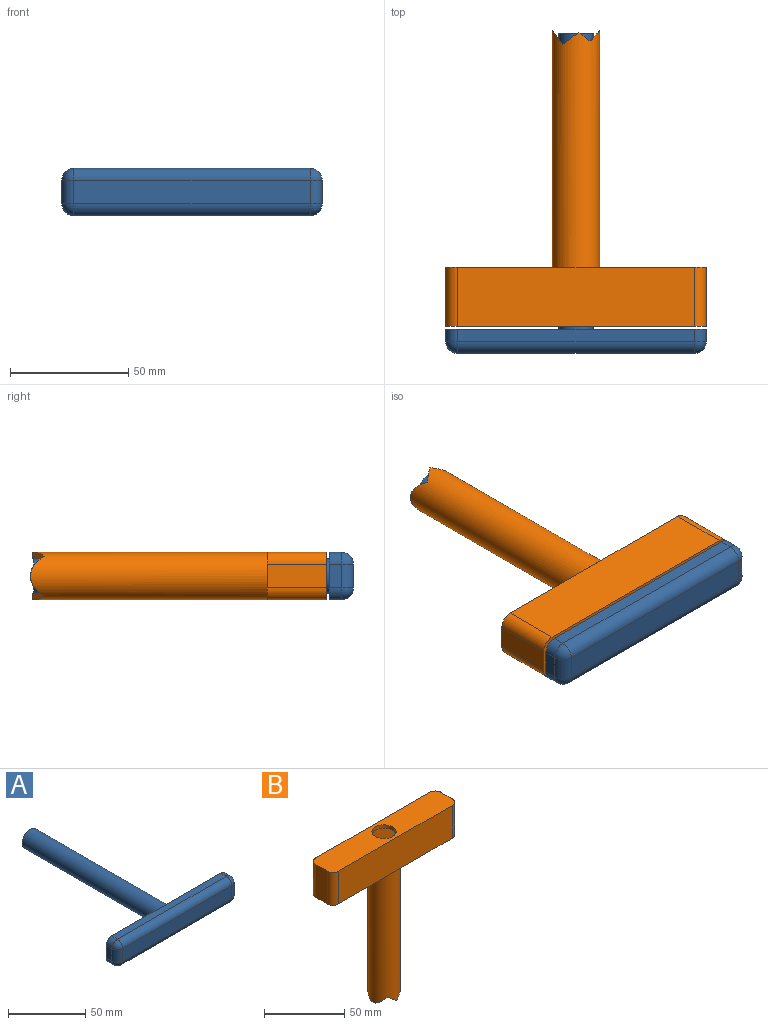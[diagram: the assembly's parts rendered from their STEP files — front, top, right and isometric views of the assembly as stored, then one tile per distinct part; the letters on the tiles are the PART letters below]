
ASSEMBLY  parts=2 mates=1
PART A: 20 faces, bbox 110x135.2x20 mm
  f0: cylinder r=7.25mm len=125mm, axis (0,1,0), area 5694.1mm2, adj f1,f4
  f1: plane 14.5x14.5mm, normal (0,1,0), area 165.1mm2, adj f0
  f2: plane 100x10mm, normal (0,-1,0), area 1000mm2, adj f8,f9,f10,f11
  f3: plane 100x5.23mm, normal (0,0,-1), area 523.4mm2, adj f4,f11,f16,f18
  f4: plane 110x20mm, normal (0,1,0), area 2013.4mm2, adj f0,f3,f5,f6,f7,f12,f14,f16
  f5: plane 100x5.23mm, normal (0,0,1), area 523.4mm2, adj f4,f8,f12,f14
  f6: plane 10x5.23mm, normal (1,0,0), area 52.3mm2, adj f4,f9,f12,f16
  f7: plane 10x5.23mm, normal (-1,0,0), area 52.3mm2, adj f4,f10,f14,f18
  f8: cylinder r=5mm len=100mm, axis (-1,0,0), area 785.4mm2, adj f2,f5,f13,f15
  f9: cylinder r=5mm len=10mm, axis (0,0,1), area 78.5mm2, adj f2,f6,f13,f17
  f10: cylinder r=5mm len=10mm, axis (0,0,-1), area 78.5mm2, adj f2,f7,f15,f19
  f11: cylinder r=5mm len=100mm, axis (1,0,0), area 785.4mm2, adj f2,f3,f17,f19
  f12: cylinder r=5mm len=5.23mm, axis (0,1,0), area 41.1mm2, adj f4,f5,f6,f13
  f13: sphere r=5mm, area 39.3mm2, adj f8,f9,f12
  f14: cylinder r=5mm len=5.23mm, axis (0,-1,0), area 41.1mm2, adj f4,f5,f7,f15
  f15: sphere r=5mm, area 39.3mm2, adj f8,f10,f14
  f16: cylinder r=5mm len=5.23mm, axis (0,-1,0), area 41.1mm2, adj f3,f4,f6,f17
  f17: sphere r=5mm, area 39.3mm2, adj f9,f11,f16
  f18: cylinder r=5mm len=5.23mm, axis (0,1,0), area 41.1mm2, adj f3,f4,f7,f19
  f19: sphere r=5mm, area 39.3mm2, adj f10,f11,f18
PART B: 29 faces, bbox 110x20x125 mm
  f0: cylinder r=7.5mm len=101.75mm, axis (0,0,1), area 4664mm2, adj f4,f5,f19,f20,f21,f22,f23,f24
  f1: plane 1.8x0.04mm, normal (0,0,-1), area 0mm2, adj f2,f19
  f2: cylinder r=10mm len=100mm, axis (0,0,1), area 6134.7mm2, adj f1,f12,f13,f19,f20,f21,f22,f23
  f3: plane 52.5x15mm, normal (0,0,-1), area 699.1mm2, adj f6,f7,f9,f11
  f4: plane 52.5x15mm, normal (0,0,1), area 699.1mm2, adj f0,f6,f7,f9
  f5: plane 52.5x15mm, normal (0,0,1), area 699.1mm2, adj f0,f7,f8,f9
  f6: plane 20x15mm, normal (1,0,0), area 300mm2, adj f3,f4,f7,f9
  f7: plane 105x20mm, normal (0,1,0), area 2100mm2, adj f3,f4,f5,f6,f8,f10
  f8: plane 20x15mm, normal (-1,0,0), area 300mm2, adj f5,f7,f9,f10
  f9: plane 105x20mm, normal (0,-1,0), area 2100mm2, adj f3,f4,f5,f6,f8,f10
  f10: plane 52.5x15mm, normal (0,0,-1), area 699.1mm2, adj f7,f8,f9,f11
  f11: cylinder r=7.5mm len=15mm, axis (0,0,-1), area 117.8mm2, adj f3,f10,f18
  f12: plane 55x20mm, normal (0,0,-1), area 932.2mm2, adj f2,f14,f15,f17,f25,f26
  f13: plane 55x20mm, normal (0,0,-1), area 932.2mm2, adj f2,f15,f16,f17,f27,f28
  f14: plane 25x10mm, normal (-1,0,0), area 250mm2, adj f12,f18,f25,f26
  f15: plane 100x25mm, normal (0,-1,0), area 2500mm2, adj f12,f13,f18,f25,f27
  f16: plane 25x10mm, normal (1,0,0), area 250mm2, adj f13,f18,f27,f28
  f17: plane 100x25mm, normal (0,1,0), area 2500mm2, adj f12,f13,f18,f26,f28
  f18: plane 110x20mm, normal (0,0,1), area 2001.8mm2, adj f11,f14,f15,f16,f17,f25,f26,f27
  f19: plane 16.12x4.78mm, normal (-0.76,0,-0.65), area 55.8mm2, adj f0,f1,f2,f20,f21
  f20: plane 5.32x4.76mm, normal (0.65,0,-0.76), area 17.6mm2, adj f0,f2,f19,f23
  f21: plane 5.32x4.76mm, normal (0.65,0,-0.76), area 17.6mm2, adj f0,f2,f19,f22
  f22: plane 6.66x5.16mm, normal (-0.61,0,-0.79), area 22.5mm2, adj f0,f2,f21,f24
  f23: plane 6.66x5.16mm, normal (-0.61,0,-0.79), area 22.5mm2, adj f0,f2,f20,f24
  f24: plane 16.7x5.81mm, normal (0.79,0,-0.61), area 63.5mm2, adj f0,f2,f22,f23
  f25: cylinder r=5mm len=25mm, axis (0,0,1), area 196.3mm2, adj f12,f14,f15,f18
  f26: cylinder r=5mm len=25mm, axis (0,0,-1), area 196.3mm2, adj f12,f14,f17,f18
  f27: cylinder r=5mm len=25mm, axis (0,0,-1), area 196.3mm2, adj f13,f15,f16,f18
  f28: cylinder r=5mm len=25mm, axis (0,0,1), area 196.3mm2, adj f13,f16,f17,f18
PLACE A t=(17.85,1.49,-101.43)mm
PLACE B rot(axis=(1,0,0),90deg) t=(17.85,-97.2,-101.43)mm fixed
MATE slider A.f0 <-> B.f0  axis (0,1,0) through (17.85,-61.01,-101.43)mm
